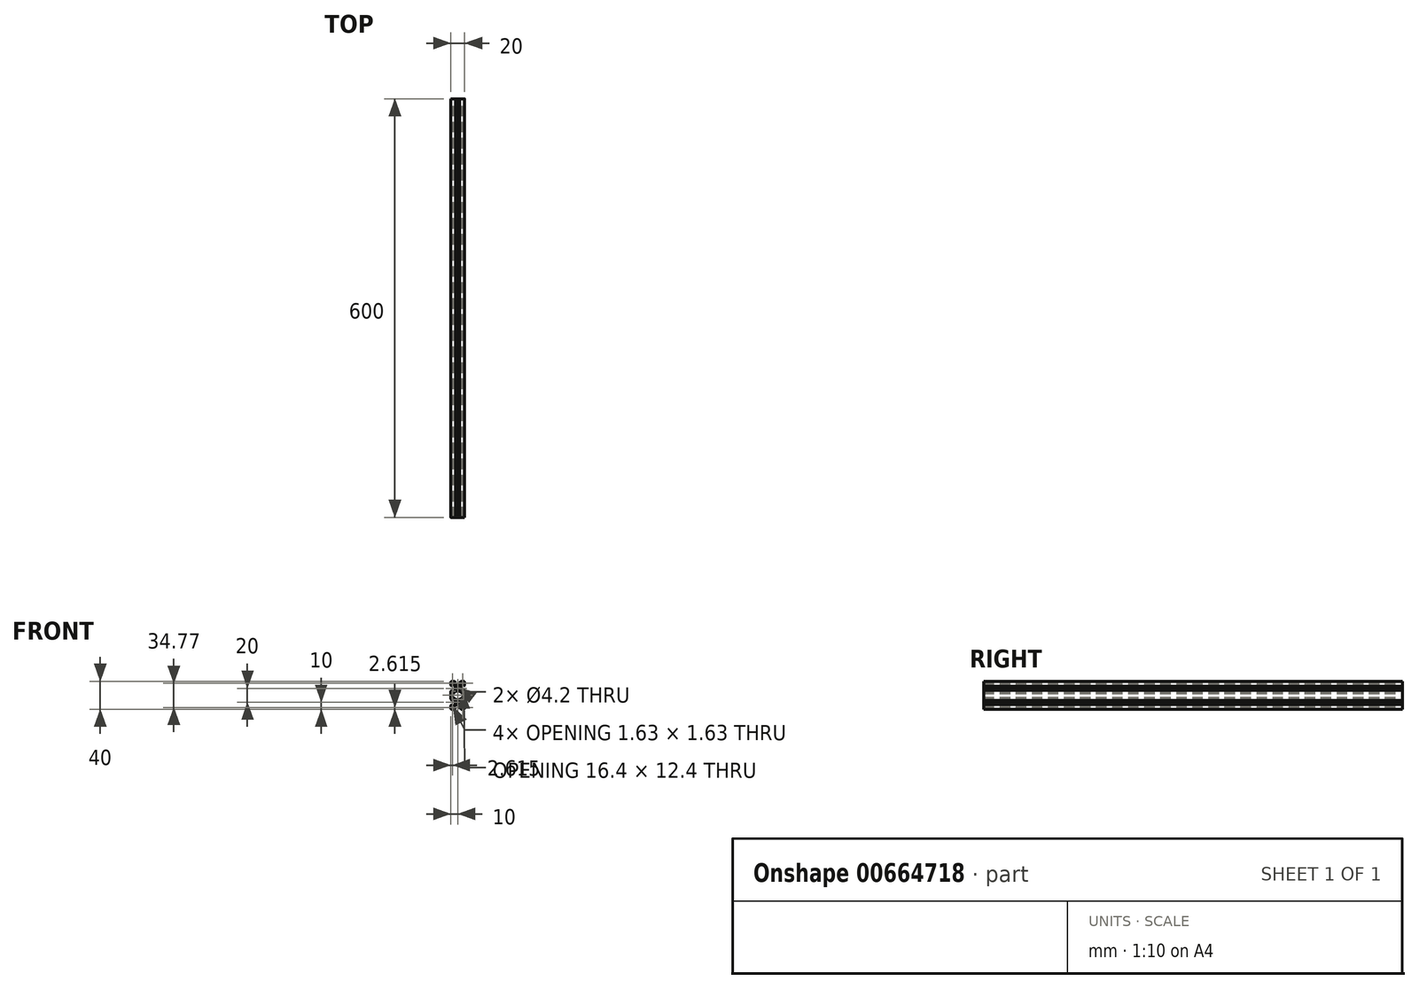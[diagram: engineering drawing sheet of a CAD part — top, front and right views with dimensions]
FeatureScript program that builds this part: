
annotation { "Feature Type Name" : "Feature", "Feature Type Description" : "" }
export const myFeature = defineFeature(function(context is Context, id is Id, definition is map)
    precondition{}
    {
        {
            var Q0;
            Q0=qCreatedBy(makeId("Front.planeOp"),FACE);
            var sketch = newSketch(context, id + "F0", { "sketchPlane" : qUnion([Q0])});
            skLineSegment(sketch, "E0", {"start": v(1.5, 0) * mm, "end": v(5.1, 0) * mm});
            skLineSegment(sketch, "E1", {"start": v(0, -1.5) * mm, "end": v(0, -5.1) * mm});
            skLineSegment(sketch, "E2", {"start": v(5.65, -0.23) * mm, "end": v(7.11, -1.69) * mm});
            skLineSegment(sketch, "E3", {"start": v(7.11, -1.7) * mm, "end": v(7.11, -1.8) * mm});
            skLineSegment(sketch, "E4", {"start": v(0.23, -5.65) * mm, "end": v(1.69, -7.11) * mm});
            skLineSegment(sketch, "E5", {"start": v(1.7, -7.11) * mm, "end": v(1.8, -7.11) * mm});
            skLineSegment(sketch, "E6", {"start": v(1.8, -7.11) * mm, "end": v(1.8, -4.5) * mm});
            skLineSegment(sketch, "E7", {"start": v(1.8, -4.5) * mm, "end": v(3.44, -4.5) * mm});
            skLineSegment(sketch, "E8", {"start": v(7.11, -1.8) * mm, "end": v(4.5, -1.8) * mm});
            skLineSegment(sketch, "E9", {"start": v(4.5, -1.8) * mm, "end": v(4.5, -3.44) * mm});
            skPoint(sketch, "E10.visualSharp", {"position": v(0, 0) * mm});
            skArc(sketch, "E10.filletArc", {"start": v(1.5, 0) * mm, "mid": v(0.44, -0.44) * mm, "end": v(0, -1.5) * mm});
            skPoint(sketch, "E11.visualSharp", {"position": v(5.42, 0) * mm});
            skArc(sketch, "E11.filletArc", {"start": v(5.65, -0.23) * mm, "mid": v(5.4, -0.06) * mm, "end": v(5.1, 0) * mm});
            skPoint(sketch, "E12.visualSharp", {"position": v(0, -5.42) * mm});
            skArc(sketch, "E12.filletArc", {"start": v(0, -5.1) * mm, "mid": v(0.06, -5.4) * mm, "end": v(0.23, -5.65) * mm});
            skLineSegment(sketch, "E13", {"start": v(1.8, -4.5) * mm, "end": v(1.8, 0) * mm, "construction": true});
            skLineSegment(sketch, "E14", {"start": v(4.5, -1.8) * mm, "end": v(0, -1.8) * mm, "construction": true});
            skPoint(sketch, "E15", {"position": v(1.8, -1.8) * mm});
            skLineSegment(sketch, "E16", {"start": v(1.8, -1.8) * mm, "end": v(3.43, -1.8) * mm});
            skLineSegment(sketch, "E17", {"start": v(3.43, -1.8) * mm, "end": v(3.43, -2.34) * mm});
            skLineSegment(sketch, "E18", {"start": v(1.8, -1.8) * mm, "end": v(1.8, -3.43) * mm});
            skLineSegment(sketch, "E19", {"start": v(1.8, -3.43) * mm, "end": v(2.34, -3.43) * mm});
            skLineSegment(sketch, "E20", {"start": v(2.34, -3.43) * mm, "end": v(3.43, -2.34) * mm});
            skArc(sketch, "E21", {"start": v(10, -7.9) * mm, "mid": v(8.52, -8.52) * mm, "end": v(7.9, -10) * mm});
            skLineSegment(sketch, "E22", {"start": v(10, -7.9) * mm, "end": v(10, -6.2) * mm, "construction": true});
            skLineSegment(sketch, "E23", {"start": v(9.9, -6.1) * mm, "end": v(7.16, -6.1) * mm});
            skLineSegment(sketch, "E24", {"start": v(7.16, -6.1) * mm, "end": v(4.5, -3.44) * mm});
            skLineSegment(sketch, "E25", {"start": v(7.9, -10) * mm, "end": v(6.2, -10) * mm, "construction": true});
            skLineSegment(sketch, "E26", {"start": v(6.1, -9.9) * mm, "end": v(6.1, -7.16) * mm});
            skLineSegment(sketch, "E27", {"start": v(6.1, -7.16) * mm, "end": v(3.44, -4.5) * mm});
            skLineSegment(sketch, "E28", {"start": v(1.8, -1.8) * mm, "end": v(10, -10) * mm, "construction": true});
            skLineSegment(sketch, "E29", {"start": v(6.2, -10) * mm, "end": v(6.1, -9.9) * mm});
            skLineSegment(sketch, "E30", {"start": v(10, -6.2) * mm, "end": v(9.9, -6.1) * mm});
            skArc(sketch, "E31", {"start": v(7.9, -10) * mm, "mid": v(8.52, -11.48) * mm, "end": v(10, -12.1) * mm});
            skLineSegment(sketch, "E32", {"start": v(6.2, -10) * mm, "end": v(6.1, -10.1) * mm});
            skLineSegment(sketch, "E33", {"start": v(6.1, -10.1) * mm, "end": v(6.1, -12.84) * mm});
            skLineSegment(sketch, "E34", {"start": v(10, -12.1) * mm, "end": v(10, -13.8) * mm, "construction": true});
            skLineSegment(sketch, "E35", {"start": v(10, -13.8) * mm, "end": v(9.9, -13.9) * mm});
            skLineSegment(sketch, "E36", {"start": v(9.9, -13.9) * mm, "end": v(7.16, -13.9) * mm});
            skLineSegment(sketch, "E37", {"start": v(6.1, -12.84) * mm, "end": v(7.16, -13.9) * mm, "construction": true});
            skLineSegment(sketch, "E38", {"start": v(7.16, -6.1) * mm, "end": v(6.1, -7.16) * mm, "construction": true});
            skLineSegment(sketch, "E39", {"start": v(6.1, -12.84) * mm, "end": v(3.44, -15.5) * mm});
            skLineSegment(sketch, "E40", {"start": v(7.16, -13.9) * mm, "end": v(3.76, -17.3) * mm});
            skLineSegment(sketch, "E41", {"start": v(10, -10) * mm, "end": v(1.8, -18.2) * mm, "construction": true});
            skLineSegment(sketch, "E42", {"start": v(3.44, -15.5) * mm, "end": v(1.8, -15.5) * mm});
            skLineSegment(sketch, "E43", {"start": v(1.8, -15.5) * mm, "end": v(1.8, -12.89) * mm});
            skLineSegment(sketch, "E44", {"start": v(1.8, -12.89) * mm, "end": v(1.7, -12.89) * mm});
            skLineSegment(sketch, "E45", {"start": v(1.7, -12.89) * mm, "end": v(0.23, -14.35) * mm});
            skLineSegment(sketch, "E46", {"start": v(0, -14.9) * mm, "end": v(0, -20) * mm});
            skLineSegment(sketch, "E47", {"start": v(0, -20) * mm, "end": v(1.8, -20) * mm, "construction": true});
            skLineSegment(sketch, "E48", {"start": v(1.8, -20) * mm, "end": v(1.8, -17.3) * mm});
            skLineSegment(sketch, "E49", {"start": v(1.8, -17.3) * mm, "end": v(3.76, -17.3) * mm});
            skPoint(sketch, "E50.visualSharp", {"position": v(0, -14.58) * mm});
            skArc(sketch, "E50.filletArc", {"start": v(0.23, -14.35) * mm, "mid": v(0.06, -14.6) * mm, "end": v(0, -14.9) * mm});
            skLineSegment(sketch, "E51.MirrorCS", {"start": v(13.8, -10) * mm, "end": v(13.9, -10.1) * mm});
            skLineSegment(sketch, "E52.MirrorCS", {"start": v(13.8, -10) * mm, "end": v(13.9, -9.9) * mm});
            skLineSegment(sketch, "E53.MirrorCS", {"start": v(12.9, -1.69) * mm, "end": v(12.9, -1.8) * mm});
            skLineSegment(sketch, "E54.MirrorCS", {"start": v(16.57, -1.8) * mm, "end": v(16.57, -2.34) * mm});
            skLineSegment(sketch, "E55.MirrorCS", {"start": v(10, -13.8) * mm, "end": v(10.1, -13.9) * mm});
            skLineSegment(sketch, "E56.MirrorCS", {"start": v(12.84, -6.1) * mm, "end": v(13.9, -7.16) * mm, "construction": true});
            skArc(sketch, "E57.MirrorCS", {"start": v(14.35, -0.23) * mm, "mid": v(14.6, -0.06) * mm, "end": v(14.9, 0) * mm});
            skArc(sketch, "E58.MirrorCS", {"start": v(20, -5.1) * mm, "mid": v(19.94, -5.4) * mm, "end": v(19.77, -5.65) * mm});
            skLineSegment(sketch, "E59.MirrorCS", {"start": v(13.9, -12.84) * mm, "end": v(12.84, -13.9) * mm, "construction": true});
            skArc(sketch, "E60.MirrorCS", {"start": v(19.77, -14.35) * mm, "mid": v(19.94, -14.6) * mm, "end": v(20, -14.9) * mm});
            skLineSegment(sketch, "E61.MirrorCS", {"start": v(18.31, -7.11) * mm, "end": v(18.2, -7.11) * mm});
            skLineSegment(sketch, "E62.MirrorCS", {"start": v(10, -6.2) * mm, "end": v(10.1, -6.1) * mm});
            skLineSegment(sketch, "E63.MirrorCS", {"start": v(18.2, -3.43) * mm, "end": v(17.66, -3.43) * mm});
            skLineSegment(sketch, "E64.MirrorCS", {"start": v(18.2, -12.89) * mm, "end": v(18.31, -12.89) * mm});
            skLineSegment(sketch, "E65.MirrorCS", {"start": v(17.66, -3.43) * mm, "end": v(16.57, -2.34) * mm});
            skLineSegment(sketch, "E66.MirrorCS", {"start": v(18.31, -12.89) * mm, "end": v(19.77, -14.35) * mm});
            skLineSegment(sketch, "E67.MirrorCS", {"start": v(18.2, -1.8) * mm, "end": v(16.57, -1.8) * mm});
            skArc(sketch, "E68.MirrorCS", {"start": v(18.5, 0) * mm, "mid": v(19.56, -0.44) * mm, "end": v(20, -1.5) * mm});
            skLineSegment(sketch, "E69.MirrorCS", {"start": v(15.5, -1.8) * mm, "end": v(15.5, -3.44) * mm});
            skLineSegment(sketch, "E70.MirrorCS", {"start": v(12.1, -10) * mm, "end": v(13.8, -10) * mm, "construction": true});
            skLineSegment(sketch, "E71.MirrorCS", {"start": v(18.2, -1.8) * mm, "end": v(18.2, -3.43) * mm});
            skPoint(sketch, "E72.MirrorP", {"position": v(18.2, -1.8) * mm});
            skLineSegment(sketch, "E73.MirrorCS", {"start": v(10.1, -6.1) * mm, "end": v(12.84, -6.1) * mm});
            skLineSegment(sketch, "E74.MirrorCS", {"start": v(20, -20) * mm, "end": v(18.2, -20) * mm, "construction": true});
            skLineSegment(sketch, "E75.MirrorCS", {"start": v(18.2, -7.11) * mm, "end": v(18.2, -4.5) * mm});
            skLineSegment(sketch, "E76.MirrorCS", {"start": v(18.5, 0) * mm, "end": v(14.9, 0) * mm});
            skLineSegment(sketch, "E77.MirrorCS", {"start": v(12.84, -6.1) * mm, "end": v(15.5, -3.44) * mm});
            skArc(sketch, "E78.MirrorCS", {"start": v(12.1, -10) * mm, "mid": v(11.48, -11.48) * mm, "end": v(10, -12.1) * mm});
            skLineSegment(sketch, "E79.MirrorCS", {"start": v(12.84, -13.9) * mm, "end": v(16.24, -17.3) * mm});
            skLineSegment(sketch, "E80.MirrorCS", {"start": v(13.9, -7.16) * mm, "end": v(16.56, -4.5) * mm});
            skLineSegment(sketch, "E81.MirrorCS", {"start": v(20, -14.9) * mm, "end": v(20, -20) * mm});
            skLineSegment(sketch, "E82.MirrorCS", {"start": v(13.9, -12.84) * mm, "end": v(16.56, -15.5) * mm});
            skLineSegment(sketch, "E83.MirrorCS", {"start": v(18.2, -20) * mm, "end": v(18.2, -17.3) * mm});
            skLineSegment(sketch, "E84.MirrorCS", {"start": v(14.35, -0.23) * mm, "end": v(12.9, -1.69) * mm});
            skPoint(sketch, "E85.MirrorP", {"position": v(20, 0) * mm});
            skLineSegment(sketch, "E86.MirrorCS", {"start": v(18.2, -4.5) * mm, "end": v(16.56, -4.5) * mm});
            skLineSegment(sketch, "E87.MirrorCS", {"start": v(12.9, -1.8) * mm, "end": v(15.5, -1.8) * mm});
            skPoint(sketch, "E88.MirrorP", {"position": v(20, -14.58) * mm});
            skLineSegment(sketch, "E89.MirrorCS", {"start": v(20, -1.5) * mm, "end": v(20, -5.1) * mm});
            skLineSegment(sketch, "E90.MirrorCS", {"start": v(18.2, -15.5) * mm, "end": v(18.2, -12.89) * mm});
            skLineSegment(sketch, "E91.MirrorCS", {"start": v(16.56, -15.5) * mm, "end": v(18.2, -15.5) * mm});
            skLineSegment(sketch, "E92.MirrorCS", {"start": v(13.9, -9.9) * mm, "end": v(13.9, -7.16) * mm});
            skArc(sketch, "E93.MirrorCS", {"start": v(10, -7.9) * mm, "mid": v(11.48, -8.52) * mm, "end": v(12.1, -10) * mm});
            skPoint(sketch, "E94.MirrorP", {"position": v(14.58, 0) * mm});
            skLineSegment(sketch, "E95.MirrorCS", {"start": v(18.2, -4.5) * mm, "end": v(18.2, 0) * mm, "construction": true});
            skLineSegment(sketch, "E96.MirrorCS", {"start": v(15.5, -1.8) * mm, "end": v(20, -1.8) * mm, "construction": true});
            skLineSegment(sketch, "E97.MirrorCS", {"start": v(10, -10) * mm, "end": v(18.2, -18.2) * mm, "construction": true});
            skLineSegment(sketch, "E98.MirrorCS", {"start": v(18.2, -17.3) * mm, "end": v(16.24, -17.3) * mm});
            skLineSegment(sketch, "E99.MirrorCS", {"start": v(18.2, -1.8) * mm, "end": v(10, -10) * mm, "construction": true});
            skLineSegment(sketch, "E100.MirrorCS", {"start": v(10.1, -13.9) * mm, "end": v(12.84, -13.9) * mm});
            skPoint(sketch, "E101.MirrorP", {"position": v(20, -5.42) * mm});
            skLineSegment(sketch, "E102.MirrorCS", {"start": v(19.77, -5.65) * mm, "end": v(18.31, -7.11) * mm});
            skLineSegment(sketch, "E103.MirrorCS", {"start": v(13.9, -10.1) * mm, "end": v(13.9, -12.84) * mm});
            skLineSegment(sketch, "E104.MirrorCS", {"start": v(6.2, -30) * mm, "end": v(6.1, -29.9) * mm});
            skLineSegment(sketch, "E105.MirrorCS", {"start": v(6.2, -30) * mm, "end": v(6.1, -30.1) * mm});
            skLineSegment(sketch, "E106.MirrorCS", {"start": v(13.8, -30) * mm, "end": v(13.9, -30.1) * mm});
            skLineSegment(sketch, "E107.MirrorCS", {"start": v(13.8, -30) * mm, "end": v(13.9, -29.9) * mm});
            skLineSegment(sketch, "E108.MirrorCS", {"start": v(10, -26.2) * mm, "end": v(9.9, -26.1) * mm});
            skLineSegment(sketch, "E109.MirrorCS", {"start": v(10, -26.2) * mm, "end": v(10.1, -26.1) * mm});
            skArc(sketch, "E110.MirrorCS", {"start": v(14.35, -39.77) * mm, "mid": v(14.6, -39.94) * mm, "end": v(14.9, -40) * mm});
            skLineSegment(sketch, "E111.MirrorCS", {"start": v(10, -33.8) * mm, "end": v(9.9, -33.9) * mm});
            skArc(sketch, "E112.MirrorCS", {"start": v(0.23, -25.65) * mm, "mid": v(0.06, -25.4) * mm, "end": v(0, -25.1) * mm});
            skArc(sketch, "E113.MirrorCS", {"start": v(19.77, -25.65) * mm, "mid": v(19.94, -25.4) * mm, "end": v(20, -25.1) * mm});
            skArc(sketch, "E114.MirrorCS", {"start": v(5.65, -39.77) * mm, "mid": v(5.4, -39.94) * mm, "end": v(5.1, -40) * mm});
            skLineSegment(sketch, "E115.MirrorCS", {"start": v(10, -33.8) * mm, "end": v(10.1, -33.9) * mm});
            skLineSegment(sketch, "E116.MirrorCS", {"start": v(7.11, -38.3) * mm, "end": v(7.11, -38.2) * mm});
            skLineSegment(sketch, "E117.MirrorCS", {"start": v(18.2, -36.57) * mm, "end": v(17.66, -36.57) * mm});
            skArc(sketch, "E118.MirrorCS", {"start": v(0, -34.9) * mm, "mid": v(0.06, -34.6) * mm, "end": v(0.23, -34.35) * mm});
            skLineSegment(sketch, "E119.MirrorCS", {"start": v(1.8, -36.57) * mm, "end": v(2.34, -36.57) * mm});
            skLineSegment(sketch, "E120.MirrorCS", {"start": v(3.43, -38.2) * mm, "end": v(3.43, -37.66) * mm});
            skLineSegment(sketch, "E121.MirrorCS", {"start": v(1.8, -27.11) * mm, "end": v(1.7, -27.11) * mm});
            skLineSegment(sketch, "E122.MirrorCS", {"start": v(18.31, -32.89) * mm, "end": v(18.2, -32.89) * mm});
            skLineSegment(sketch, "E123.MirrorCS", {"start": v(12.9, -38.31) * mm, "end": v(12.9, -38.2) * mm});
            skLineSegment(sketch, "E124.MirrorCS", {"start": v(16.57, -38.2) * mm, "end": v(16.57, -37.66) * mm});
            skLineSegment(sketch, "E125.MirrorCS", {"start": v(10, -27.9) * mm, "end": v(10, -26.2) * mm, "construction": true});
            skLineSegment(sketch, "E126.MirrorCS", {"start": v(1.7, -32.9) * mm, "end": v(1.8, -32.9) * mm});
            skLineSegment(sketch, "E127.MirrorCS", {"start": v(18.2, -27.11) * mm, "end": v(18.31, -27.11) * mm});
            skArc(sketch, "E128.MirrorCS", {"start": v(20, -34.9) * mm, "mid": v(19.94, -34.6) * mm, "end": v(19.77, -34.35) * mm});
            skLineSegment(sketch, "E129.MirrorCS", {"start": v(2.34, -36.57) * mm, "end": v(3.43, -37.66) * mm});
            skLineSegment(sketch, "E130.MirrorCS", {"start": v(13.9, -27.16) * mm, "end": v(12.84, -26.1) * mm, "construction": true});
            skLineSegment(sketch, "E131.MirrorCS", {"start": v(1.8, -38.2) * mm, "end": v(3.43, -38.2) * mm});
            skLineSegment(sketch, "E132.MirrorCS", {"start": v(1.69, -27.11) * mm, "end": v(0.23, -25.65) * mm});
            skLineSegment(sketch, "E133.MirrorCS", {"start": v(17.66, -36.57) * mm, "end": v(16.57, -37.66) * mm});
            skLineSegment(sketch, "E134.MirrorCS", {"start": v(4.5, -38.2) * mm, "end": v(4.5, -36.56) * mm});
            skLineSegment(sketch, "E135.MirrorCS", {"start": v(6.1, -27.16) * mm, "end": v(7.16, -26.1) * mm, "construction": true});
            skLineSegment(sketch, "E136.MirrorCS", {"start": v(1.8, -38.2) * mm, "end": v(1.8, -36.57) * mm});
            skLineSegment(sketch, "E137.MirrorCS", {"start": v(18.2, -38.2) * mm, "end": v(18.2, -36.57) * mm});
            skLineSegment(sketch, "E138.MirrorCS", {"start": v(18.2, -38.2) * mm, "end": v(16.57, -38.2) * mm});
            skPoint(sketch, "E139.MirrorP", {"position": v(20, -40) * mm});
            skLineSegment(sketch, "E140.MirrorCS", {"start": v(18.2, -22.7) * mm, "end": v(16.24, -22.7) * mm});
            skLineSegment(sketch, "E141.MirrorCS", {"start": v(7.16, -26.1) * mm, "end": v(3.76, -22.7) * mm});
            skPoint(sketch, "E142.MirrorP", {"position": v(18.2, -38.2) * mm});
            skPoint(sketch, "E143.MirrorP", {"position": v(14.58, -40) * mm});
            skLineSegment(sketch, "E144.MirrorCS", {"start": v(6.1, -32.84) * mm, "end": v(3.44, -35.5) * mm});
            skArc(sketch, "E145.MirrorCS", {"start": v(18.5, -40) * mm, "mid": v(19.56, -39.56) * mm, "end": v(20, -38.5) * mm});
            skLineSegment(sketch, "E146.MirrorCS", {"start": v(16.56, -24.5) * mm, "end": v(18.2, -24.5) * mm});
            skLineSegment(sketch, "E147.MirrorCS", {"start": v(19.77, -34.35) * mm, "end": v(18.31, -32.89) * mm});
            skLineSegment(sketch, "E148.MirrorCS", {"start": v(18.5, -40) * mm, "end": v(14.9, -40) * mm});
            skArc(sketch, "E149.MirrorCS", {"start": v(12.1, -30) * mm, "mid": v(11.48, -28.52) * mm, "end": v(10, -27.9) * mm});
            skLineSegment(sketch, "E150.MirrorCS", {"start": v(7.16, -33.9) * mm, "end": v(4.5, -36.56) * mm});
            skLineSegment(sketch, "E151.MirrorCS", {"start": v(12.1, -30) * mm, "end": v(13.8, -30) * mm, "construction": true});
            skLineSegment(sketch, "E152.MirrorCS", {"start": v(1.8, -35.5) * mm, "end": v(1.8, -40) * mm, "construction": true});
            skLineSegment(sketch, "E153.MirrorCS", {"start": v(18.2, -38.2) * mm, "end": v(10, -30) * mm, "construction": true});
            skLineSegment(sketch, "E154.MirrorCS", {"start": v(4.5, -38.2) * mm, "end": v(0, -38.2) * mm, "construction": true});
            skLineSegment(sketch, "E155.MirrorCS", {"start": v(10, -30) * mm, "end": v(18.2, -21.8) * mm, "construction": true});
            skLineSegment(sketch, "E156.MirrorCS", {"start": v(15.5, -38.2) * mm, "end": v(15.5, -36.56) * mm});
            skLineSegment(sketch, "E157.MirrorCS", {"start": v(1.5, -40) * mm, "end": v(5.1, -40) * mm});
            skLineSegment(sketch, "E158.MirrorCS", {"start": v(10, -32.1) * mm, "end": v(10, -33.8) * mm, "construction": true});
            skPoint(sketch, "E159.MirrorP", {"position": v(1.8, -38.2) * mm});
            skLineSegment(sketch, "E160.MirrorCS", {"start": v(7.9, -30) * mm, "end": v(6.2, -30) * mm, "construction": true});
            skArc(sketch, "E161.MirrorCS", {"start": v(1.5, -40) * mm, "mid": v(0.44, -39.56) * mm, "end": v(0, -38.5) * mm});
            skLineSegment(sketch, "E162.MirrorCS", {"start": v(12.84, -26.1) * mm, "end": v(16.24, -22.7) * mm});
            skLineSegment(sketch, "E163.MirrorCS", {"start": v(12.9, -38.2) * mm, "end": v(15.5, -38.2) * mm});
            skLineSegment(sketch, "E164.MirrorCS", {"start": v(7.11, -38.2) * mm, "end": v(4.5, -38.2) * mm});
            skLineSegment(sketch, "E165.MirrorCS", {"start": v(1.8, -35.5) * mm, "end": v(3.44, -35.5) * mm});
            skLineSegment(sketch, "E166.MirrorCS", {"start": v(7.16, -33.9) * mm, "end": v(6.1, -32.84) * mm, "construction": true});
            skLineSegment(sketch, "E167.MirrorCS", {"start": v(10.1, -33.9) * mm, "end": v(12.84, -33.9) * mm});
            skLineSegment(sketch, "E168.MirrorCS", {"start": v(13.9, -27.16) * mm, "end": v(16.56, -24.5) * mm});
            skLineSegment(sketch, "E169.MirrorCS", {"start": v(1.8, -38.2) * mm, "end": v(10, -30) * mm, "construction": true});
            skLineSegment(sketch, "E170.MirrorCS", {"start": v(12.84, -33.9) * mm, "end": v(15.5, -36.56) * mm});
            skLineSegment(sketch, "E171.MirrorCS", {"start": v(15.5, -38.2) * mm, "end": v(20, -38.2) * mm, "construction": true});
            skPoint(sketch, "E172.MirrorP", {"position": v(0, -25.42) * mm});
            skLineSegment(sketch, "E173.MirrorCS", {"start": v(18.2, -35.5) * mm, "end": v(18.2, -40) * mm, "construction": true});
            skLineSegment(sketch, "E174.MirrorCS", {"start": v(18.2, -35.5) * mm, "end": v(16.56, -35.5) * mm});
            skLineSegment(sketch, "E175.MirrorCS", {"start": v(18.2, -24.5) * mm, "end": v(18.2, -27.11) * mm});
            skLineSegment(sketch, "E176.MirrorCS", {"start": v(9.9, -33.9) * mm, "end": v(7.16, -33.9) * mm});
            skLineSegment(sketch, "E177.MirrorCS", {"start": v(13.9, -29.9) * mm, "end": v(13.9, -27.16) * mm});
            skLineSegment(sketch, "E178.MirrorCS", {"start": v(20, -38.5) * mm, "end": v(20, -34.9) * mm});
            skLineSegment(sketch, "E179.MirrorCS", {"start": v(13.9, -32.84) * mm, "end": v(16.56, -35.5) * mm});
            skLineSegment(sketch, "E180.MirrorCS", {"start": v(18.2, -20) * mm, "end": v(18.2, -22.7) * mm});
            skArc(sketch, "E181.MirrorCS", {"start": v(10, -32.1) * mm, "mid": v(8.52, -31.48) * mm, "end": v(7.9, -30) * mm});
            skLineSegment(sketch, "E182.MirrorCS", {"start": v(12.84, -33.9) * mm, "end": v(13.9, -32.84) * mm, "construction": true});
            skLineSegment(sketch, "E183.MirrorCS", {"start": v(5.65, -39.77) * mm, "end": v(7.11, -38.31) * mm});
            skLineSegment(sketch, "E184.MirrorCS", {"start": v(10, -30) * mm, "end": v(1.8, -21.8) * mm, "construction": true});
            skLineSegment(sketch, "E185.MirrorCS", {"start": v(20, -25.1) * mm, "end": v(20, -20) * mm});
            skLineSegment(sketch, "E186.MirrorCS", {"start": v(9.9, -26.1) * mm, "end": v(7.16, -26.1) * mm});
            skArc(sketch, "E187.MirrorCS", {"start": v(7.9, -30) * mm, "mid": v(8.52, -28.52) * mm, "end": v(10, -27.9) * mm});
            skLineSegment(sketch, "E188.MirrorCS", {"start": v(18.31, -27.11) * mm, "end": v(19.77, -25.65) * mm});
            skArc(sketch, "E189.MirrorCS", {"start": v(10, -32.1) * mm, "mid": v(11.48, -31.48) * mm, "end": v(12.1, -30) * mm});
            skLineSegment(sketch, "E190.MirrorCS", {"start": v(1.8, -32.9) * mm, "end": v(1.8, -35.5) * mm});
            skLineSegment(sketch, "E191.MirrorCS", {"start": v(1.8, -22.7) * mm, "end": v(3.76, -22.7) * mm});
            skLineSegment(sketch, "E192.MirrorCS", {"start": v(0, -25.1) * mm, "end": v(0, -20) * mm});
            skLineSegment(sketch, "E193.MirrorCS", {"start": v(1.8, -24.5) * mm, "end": v(1.8, -27.11) * mm});
            skLineSegment(sketch, "E194.MirrorCS", {"start": v(14.35, -39.77) * mm, "end": v(12.9, -38.31) * mm});
            skLineSegment(sketch, "E195.MirrorCS", {"start": v(10.1, -26.1) * mm, "end": v(12.84, -26.1) * mm});
            skPoint(sketch, "E196.MirrorP", {"position": v(20, -34.58) * mm});
            skPoint(sketch, "E197.MirrorP", {"position": v(0, -40) * mm});
            skPoint(sketch, "E198.MirrorP", {"position": v(20, -25.42) * mm});
            skLineSegment(sketch, "E199.MirrorCS", {"start": v(0.23, -34.35) * mm, "end": v(1.69, -32.89) * mm});
            skLineSegment(sketch, "E200.MirrorCS", {"start": v(0, -38.5) * mm, "end": v(0, -34.9) * mm});
            skLineSegment(sketch, "E201.MirrorCS", {"start": v(18.2, -32.89) * mm, "end": v(18.2, -35.5) * mm});
            skLineSegment(sketch, "E202.MirrorCS", {"start": v(1.8, -20) * mm, "end": v(1.8, -22.7) * mm});
            skLineSegment(sketch, "E203.MirrorCS", {"start": v(6.1, -29.9) * mm, "end": v(6.1, -27.16) * mm});
            skPoint(sketch, "E204.MirrorP", {"position": v(0, -34.58) * mm});
            skLineSegment(sketch, "E205.MirrorCS", {"start": v(6.1, -27.16) * mm, "end": v(3.44, -24.5) * mm});
            skLineSegment(sketch, "E206.MirrorCS", {"start": v(3.44, -24.5) * mm, "end": v(1.8, -24.5) * mm});
            skPoint(sketch, "E207.MirrorP", {"position": v(5.42, -40) * mm});
            skLineSegment(sketch, "E208.MirrorCS", {"start": v(6.1, -30.1) * mm, "end": v(6.1, -32.84) * mm});
            skLineSegment(sketch, "E209.MirrorCS", {"start": v(13.9, -30.1) * mm, "end": v(13.9, -32.84) * mm});
            skSolve(sketch);
        }
        {
            assignVariable(context, id + "F1", {"name" : "L", "anyValue" : 600 * mm});
        }
        {
            var Q0;
            Q0=qSketchRegion(id+"F0",true);
            extrude(context, id + "F2", {"entities" : qUnion([Q0]), "depth" : getVariable(context, 'L')});
        }
    });
